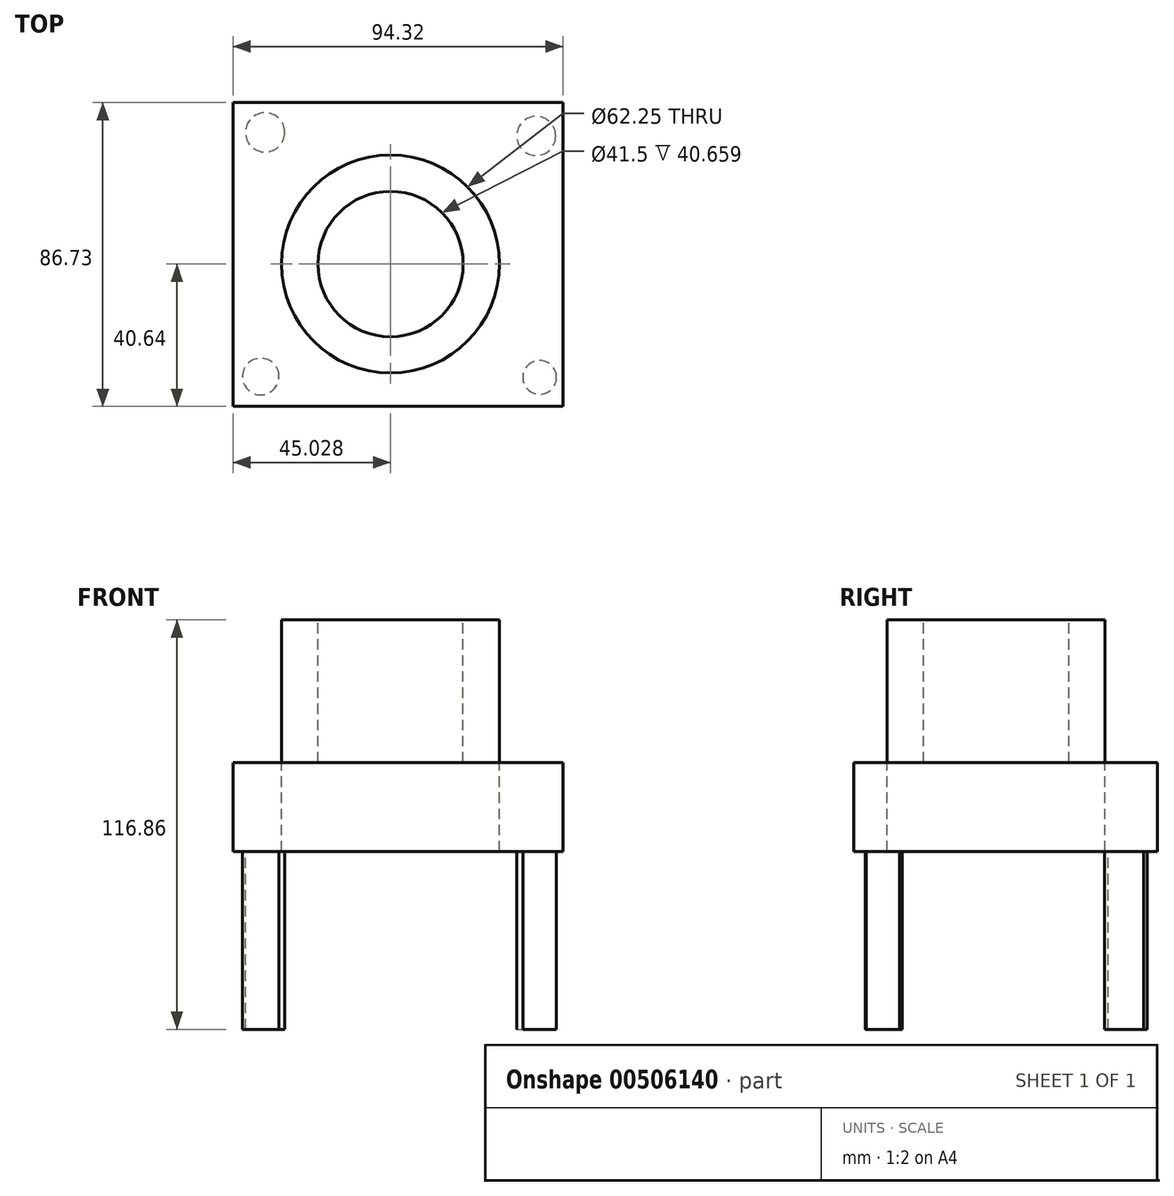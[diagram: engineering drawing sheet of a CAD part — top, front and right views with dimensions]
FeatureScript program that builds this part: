
annotation { "Feature Type Name" : "Feature", "Feature Type Description" : "" }
export const myFeature = defineFeature(function(context is Context, id is Id, definition is map)
    precondition{}
    {
        {
            var Q0;
            Q0=qCreatedBy(makeId("Front.planeOp"),FACE);
            var sketch = newSketch(context, id + "F0", { "sketchPlane" : qUnion([Q0])});
            skLineSegment(sketch, "E0", {"start": v(39.96, 57.48) * mm, "end": v(39.96, 16.82) * mm});
            skLineSegment(sketch, "E1", {"start": v(39.96, 16.82) * mm, "end": v(50.33, 16.82) * mm});
            skLineSegment(sketch, "E2", {"start": v(50.33, 16.82) * mm, "end": v(50.33, 57.48) * mm});
            skLineSegment(sketch, "E3", {"start": v(50.33, 57.48) * mm, "end": v(39.96, 57.48) * mm});
            skLineSegment(sketch, "E4", {"start": v(19.2, 55.52) * mm, "end": v(19.2, 16.26) * mm});
            skSolve(sketch);
        }
        {
            var Q0;
            Q0=makeQuery(id+"F0.imprint","IMPRINT",FACE,{"disambiguationData":[TD([[makeQuery(id+"F0.imprint","IMPRINT",EDGE,{"derivedFrom":sQuery(id+"F0.wireOp",EDGE,"E0")}),1.0]])]});
            var Q1;
            Q1=sQuery(id+"F0.wireOp",EDGE,"E4");
            revolve(context, id + "F1", {"entities" : qUnion([Q0]), "axis" : qUnion([Q1]), "revolveType" : RevolveType.FULL});
        }
        {
            var Q0;
            Q0=makeQuery(id+"F1.opRevolve","SWEPT_FACE",FACE,{"disambiguationData":[OSD([sQuery(id+"F0.wireOp",EDGE,"E1")])]});
            var sketch = newSketch(context, id + "F2", { "sketchPlane" : qUnion([Q0])});
            skLineSegment(sketch, "E5.bottom", {"start": v(-25.82, 40.64) * mm, "end": v(68.5, 40.64) * mm});
            skLineSegment(sketch, "E5.top", {"start": v(-25.82, -46.09) * mm, "end": v(68.5, -46.09) * mm});
            skLineSegment(sketch, "E5.left", {"start": v(-25.82, 40.64) * mm, "end": v(-25.82, -46.09) * mm});
            skLineSegment(sketch, "E5.right", {"start": v(68.5, 40.64) * mm, "end": v(68.5, -46.09) * mm});
            skSolve(sketch);
        }
        {
            var Q0;
            Q0=makeQuery(id+"F2.imprint","IMPRINT",FACE,{"disambiguationData":[TD([[makeQuery(id+"F2.imprint","IMPRINT",EDGE,{"derivedFrom":sQuery(id+"F2.wireOp",EDGE,"E5.bottom")}),-1.0]])]});
            extrude(context, id + "F3", {"entities" : qUnion([Q0]), "depth" : 25.4 * mm});
        }
        {
            var Q0;
            Q0=makeQuery(id+"F3.opExtrude","CAP_FACE",FACE,{"disambiguationData":[OSD([sQuery(id+"F0.wireOp",EDGE,"E1"),sQuery(id+"F0.wireOp",EDGE,"E2"),sQuery(id+"F2.wireOp",EDGE,"E5.bottom"),sQuery(id+"F2.wireOp",EDGE,"E5.top"),sQuery(id+"F2.wireOp",EDGE,"E5.left"),sQuery(id+"F2.wireOp",EDGE,"E5.right")])],"isStart":true});
            var sketch = newSketch(context, id + "F4", { "sketchPlane" : qUnion([Q0])});
            skCircle(sketch, "E6", {"center": v(58.74, 29.25) * mm, "radius": 5.8 * mm});
            skLineSegment(sketch, "E7", {"start": v(68.5, -40.64) * mm, "end": v(-25.82, 46.09) * mm});
            skSolve(sketch);
        }
        {
            var Q0;
            Q0=makeQuery(id+"F3.opExtrude","CAP_FACE",FACE,{"disambiguationData":[OSD([sQuery(id+"F0.wireOp",EDGE,"E1"),sQuery(id+"F0.wireOp",EDGE,"E2"),sQuery(id+"F2.wireOp",EDGE,"E5.bottom"),sQuery(id+"F2.wireOp",EDGE,"E5.top"),sQuery(id+"F2.wireOp",EDGE,"E5.left"),sQuery(id+"F2.wireOp",EDGE,"E5.right")])],"isStart":false});
            var sketch = newSketch(context, id + "F5", { "sketchPlane" : qUnion([Q0])});
            skCircle(sketch, "E8", {"center": v(-17.88, 32.12) * mm, "radius": 5.25 * mm});
            skCircle(sketch, "E9", {"center": v(60.81, -36.57) * mm, "radius": 5.59 * mm});
            skCircle(sketch, "E10", {"center": v(-16.63, -37.57) * mm, "radius": 5.61 * mm});
            skCircle(sketch, "E11", {"center": v(61.8, 32.37) * mm, "radius": 4.8 * mm});
            skSolve(sketch);
        }
        {
            var Q0;
            Q0=makeQuery(id+"F5.imprint","IMPRINT",FACE,{"disambiguationData":[TD([[makeQuery(id+"F5.imprint","IMPRINT",EDGE,{"derivedFrom":sQuery(id+"F5.wireOp",EDGE,"E9")}),1.0]])]});
            var Q1;
            Q1=makeQuery(id+"F5.imprint","IMPRINT",FACE,{"disambiguationData":[TD([[makeQuery(id+"F5.imprint","IMPRINT",EDGE,{"derivedFrom":sQuery(id+"F5.wireOp",EDGE,"E10")}),1.0]])]});
            var Q2;
            Q2=makeQuery(id+"F5.imprint","IMPRINT",FACE,{"disambiguationData":[TD([[makeQuery(id+"F5.imprint","IMPRINT",EDGE,{"derivedFrom":sQuery(id+"F5.wireOp",EDGE,"E8")}),1.0]])]});
            var Q3;
            Q3=makeQuery(id+"F5.imprint","IMPRINT",FACE,{"disambiguationData":[TD([[makeQuery(id+"F5.imprint","IMPRINT",EDGE,{"derivedFrom":sQuery(id+"F5.wireOp",EDGE,"E11")}),1.0]])]});
            extrude(context, id + "F6", {"entities" : qUnion([Q0, Q1, Q2, Q3]), "operationType" : NewBodyOperationType.ADD, "depth" : 50.8 * mm});
        }
    });
